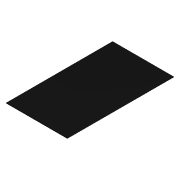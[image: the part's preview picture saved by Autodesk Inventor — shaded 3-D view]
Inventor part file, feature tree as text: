
AUTODESK INVENTOR PART (.ipt)
format: ipt  version: 2014 SP1 (Build 180222100, 222)  size: 70,144 bytes
history: native  units: in
note: dims shown in document units (in); Inventor stores cm internally (conversion verified against a paired STEP export)
features: extrude x1, sketch x1
ambient origin geometry x8: Origin, YZ Plane, XZ Plane, XY Plane, X Axis, Y Axis, Z Axis, Center Point
bodies: Solid1 (feature_tree)
feature tree (2):
  extrude  "Extrusion1"  Depth=20.0in
  sketch  "Sketch1"  dims[d0=11.5in d1=20.0in d2=0.1in d3=0.0in]
